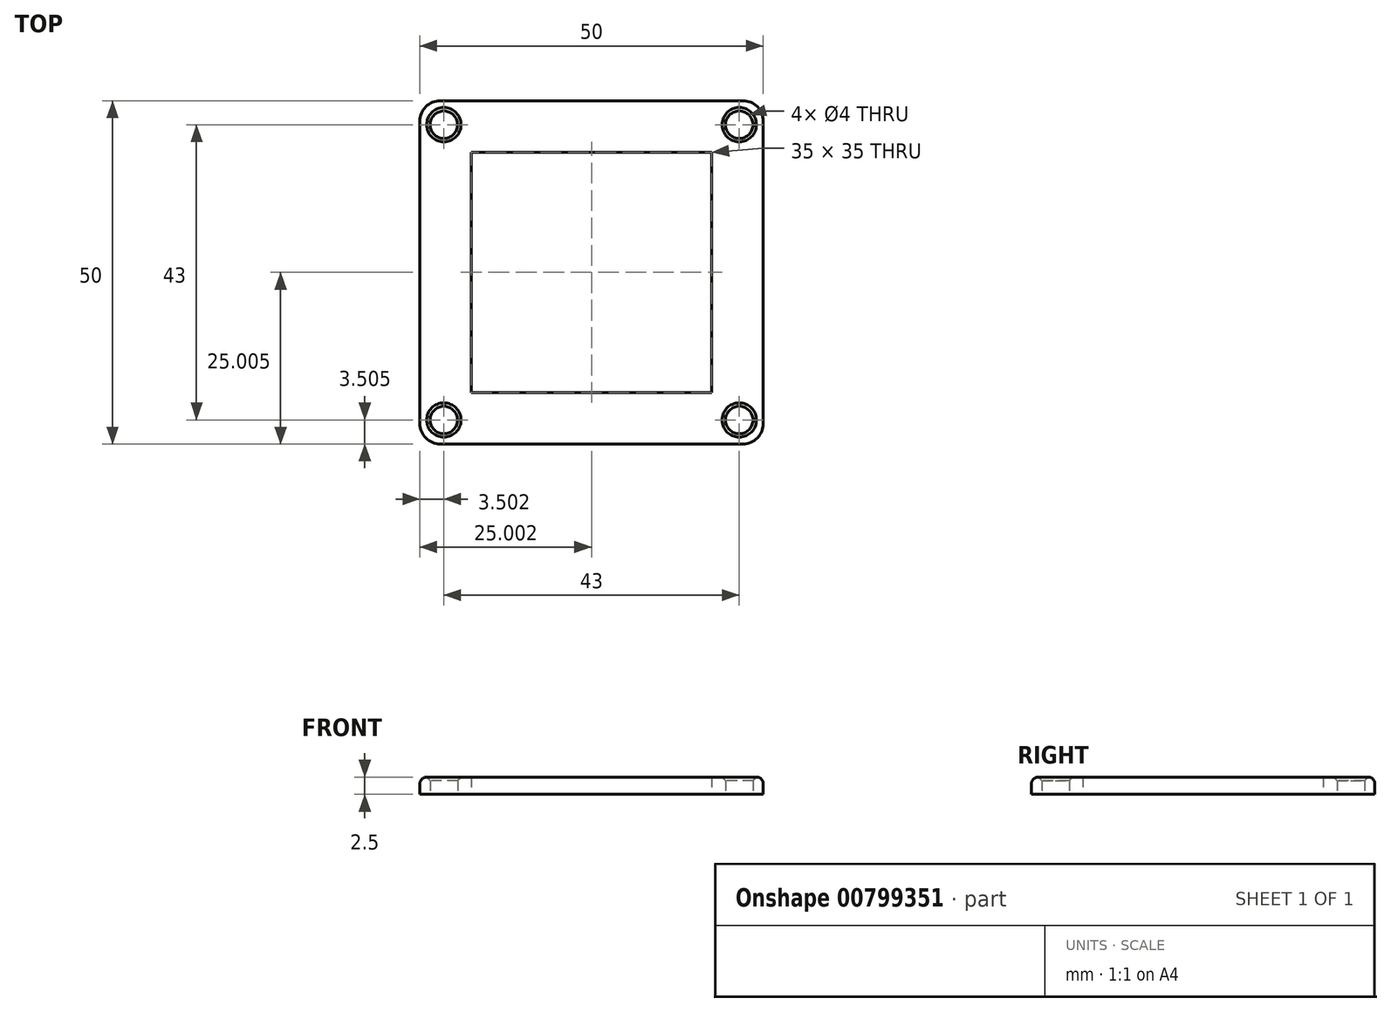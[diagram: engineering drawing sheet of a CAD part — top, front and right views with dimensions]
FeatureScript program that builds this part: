
annotation { "Feature Type Name" : "Feature", "Feature Type Description" : "" }
export const myFeature = defineFeature(function(context is Context, id is Id, definition is map)
    precondition{}
    {
        {
            var Q0;
            Q0=qCreatedBy(makeId("Top.planeOp"),FACE);
            var sketch = newSketch(context, id + "F0", { "sketchPlane" : qUnion([Q0])});
            skLineSegment(sketch, "E0.bottom", {"start": v(-13.83, 28.86) * mm, "end": v(36.17, 28.86) * mm});
            skLineSegment(sketch, "E0.top", {"start": v(-13.83, -21.14) * mm, "end": v(36.17, -21.14) * mm});
            skLineSegment(sketch, "E0.left", {"start": v(-13.83, 28.86) * mm, "end": v(-13.83, -21.14) * mm});
            skLineSegment(sketch, "E0.right", {"start": v(36.17, 28.86) * mm, "end": v(36.17, -21.14) * mm});
            skLineSegment(sketch, "E1.bottom", {"start": v(-6.33, 21.36) * mm, "end": v(28.67, 21.36) * mm});
            skLineSegment(sketch, "E1.top", {"start": v(-6.33, -13.64) * mm, "end": v(28.67, -13.64) * mm});
            skLineSegment(sketch, "E1.left", {"start": v(-6.33, 21.36) * mm, "end": v(-6.33, -13.64) * mm});
            skLineSegment(sketch, "E1.right", {"start": v(28.67, 21.36) * mm, "end": v(28.67, -13.64) * mm});
            skCircle(sketch, "E2", {"center": v(-10.33, 25.36) * mm, "radius": 2 * mm});
            skCircle(sketch, "E3", {"center": v(32.67, 25.36) * mm, "radius": 2 * mm});
            skCircle(sketch, "E4", {"center": v(-10.33, -17.64) * mm, "radius": 2 * mm});
            skCircle(sketch, "E5", {"center": v(32.67, -17.64) * mm, "radius": 2 * mm});
            skSolve(sketch);
        }
        {
            var Q0;
            Q0=makeQuery(id+"F0.imprint","IMPRINT",FACE,{"disambiguationData":[TD([[makeQuery(id+"F0.imprint","IMPRINT",EDGE,{"derivedFrom":sQuery(id+"F0.wireOp",EDGE,"E0.bottom")}),-1.0]])]});
            extrude(context, id + "F1", {"entities" : qUnion([Q0]), "depth" : 2.5 * mm, "offsetDistance" : 25 * mm});
        }
        {
            var Q0;
            Q0=makeQuery(id+"F1.opExtrude","SWEPT_EDGE",EDGE,{"disambiguationData":[OSD([sQuery(id+"F0.wireOp",EDGE,"E0.bottom"),sQuery(id+"F0.wireOp",EDGE,"E0.left")])]});
            var Q1;
            Q1=makeQuery(id+"F1.opExtrude","SWEPT_EDGE",EDGE,{"disambiguationData":[OSD([sQuery(id+"F0.wireOp",EDGE,"E0.bottom"),sQuery(id+"F0.wireOp",EDGE,"E0.right")])]});
            var Q2;
            Q2=makeQuery(id+"F1.opExtrude","SWEPT_EDGE",EDGE,{"disambiguationData":[OSD([sQuery(id+"F0.wireOp",EDGE,"E0.top"),sQuery(id+"F0.wireOp",EDGE,"E0.right")])]});
            var Q3;
            Q3=makeQuery(id+"F1.opExtrude","SWEPT_EDGE",EDGE,{"disambiguationData":[OSD([sQuery(id+"F0.wireOp",EDGE,"E0.top"),sQuery(id+"F0.wireOp",EDGE,"E0.left")])]});
            fillet(context, id + "F2", {"entities" : qUnion([Q0, Q1, Q2, Q3]), "radius" : 3 * mm, "tangentPropagation" : true, "allowEdgeOverflow" : false});
        }
        {
            var Q0;
            Q0=makeQuery(id+"F1.opExtrude","CAP_EDGE",EDGE,{"disambiguationData":[OSD([sQuery(id+"F0.wireOp",EDGE,"E2")])],"isStart":false});
            var Q1;
            Q1=makeQuery(id+"F1.opExtrude","CAP_EDGE",EDGE,{"disambiguationData":[OSD([sQuery(id+"F0.wireOp",EDGE,"E3")])],"isStart":false});
            var Q2;
            Q2=makeQuery(id+"F1.opExtrude","CAP_EDGE",EDGE,{"disambiguationData":[OSD([sQuery(id+"F0.wireOp",EDGE,"E5")])],"isStart":false});
            var Q3;
            Q3=makeQuery(id+"F1.opExtrude","CAP_EDGE",EDGE,{"disambiguationData":[OSD([sQuery(id+"F0.wireOp",EDGE,"E4")])],"isStart":false});
            chamfer(context, id + "F3", {"entities" : qUnion([Q0, Q1, Q2, Q3]), "width" : .5 * mm});
        }
        {
            var Q0;
            Q0=makeQuery(id+"F1.opExtrude","CAP_EDGE",EDGE,{"disambiguationData":[OSD([sQuery(id+"F0.wireOp",EDGE,"E0.bottom")])],"isStart":false});
            fillet(context, id + "F4", {"entities" : qUnion([Q0]), "radius" : 1 * mm, "tangentPropagation" : true, "allowEdgeOverflow" : false});
        }
    });
